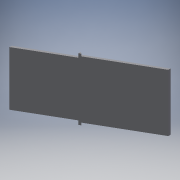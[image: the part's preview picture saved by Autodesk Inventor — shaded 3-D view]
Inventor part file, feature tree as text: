
AUTODESK INVENTOR PART (.ipt)
format: ipt  version: 2018.3 (Build 223284000, 284)  size: 3,915,776 bytes
history: native  units: mm
features: extrude x7, sketch x7, pattern_linear x2, chamfer x2
ambient origin geometry x8: Origin, YZ Plane, XZ Plane, XY Plane, X Axis, Y Axis, Z Axis, Center Point
bodies: Body1 (feature_tree)
feature tree (18):
  extrude  "Extrusion6"  Depth=150.0mm
  extrude  "Extrusion8"  Depth=3.0mm
  extrude  "Extrusion9"  Depth=3.0mm
  extrude  "Extrusion10"  Depth=2.0mm TaperAngle=0.0deg
  extrude  "Extrusion11"  Depth=3.0mm
  extrude  "Extrusion13"  Depth=2.0mm TaperAngle=0.0deg
  extrude  "Extrusion14"  Depth=4.0mm
  pattern_linear  "Rectangular Pattern3"  Spacing1=1.0mm  [1 undecoded]
  pattern_linear  "Rectangular Pattern4"  Spacing1=2.0mm  [1 undecoded]
  chamfer  "Chamfer2"  Distance=0.6mm
  chamfer  "Chamfer3"  Distance=6.0mm
  sketch  "Sketch6"  dims[d18=3.0mm d19=150.0mm]
  sketch  "Sketch8"  dims[d20=120.0deg d21=3.0mm]
  sketch  "Sketch9"  dims[d22=70.0mm d23=0.0mm d27=3.0mm]
  sketch  "Sketch10"  dims[d28=5.0mm d29=0.0mm d30=2.0mm d31=0.0mm]
  sketch  "Sketch11"  dims[d32=65.0mm d33=3.0mm]
  sketch  "Sketch12"  dims[d34=5.0mm d35=0.0mm d36=2.0mm d37=0.0mm]
  sketch  "Sketch13"  dims[d38=6.0mm d39=4.0mm d40=1.0mm d41=2.0mm d50=0.6mm d51=6.0mm d52=0.6mm d53=0.5mm d54=0.5mm d55=0.0mm d56=0.4mm d57=0.0mm d58=4.0mm d59=1.0mm d60=2.0mm d61=142.0mm d62=0.5mm d63=0.0mm d64=150.0mm d66=4.6mm d67=210.0mm d69=7.0mm d70=3.0mm d71=2.0mm d72=60.0deg d73=3.0mm d74=2.0mm d75=60.0deg]
note: 2 required parameter values undecoded (feature->parameter linkage not recoverable at this tier; creation-order binding heuristic only, values carry confidence <= 0.55)
